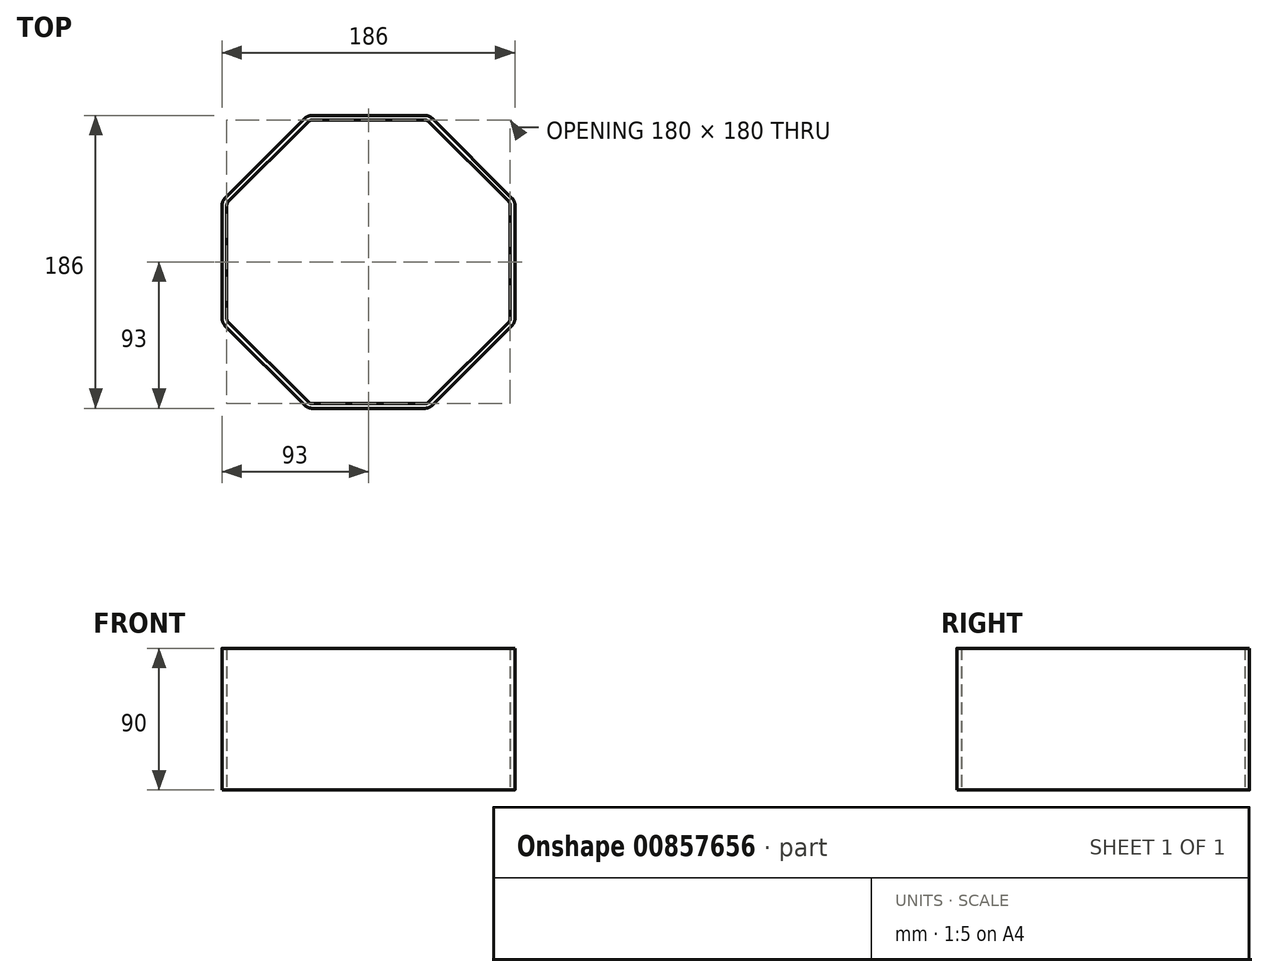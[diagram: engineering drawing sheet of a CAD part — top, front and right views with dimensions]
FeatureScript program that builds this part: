
annotation { "Feature Type Name" : "Feature", "Feature Type Description" : "" }
export const myFeature = defineFeature(function(context is Context, id is Id, definition is map)
    precondition{}
    {
        {
            var Q0;
            Q0=qCreatedBy(makeId("Top.planeOp"),FACE);
            var sketch = newSketch(context, id + "F0", { "sketchPlane" : qUnion([Q0])});
            skCircle(sketch, "E0.cCircle", {"center": v(0, 0) * mm, "radius": 90 * mm, "construction": true});
            skLineSegment(sketch, "E0.0", {"start": v(-37.28, 90) * mm, "end": v(37.28, 90) * mm});
            skLineSegment(sketch, "E0.1", {"start": v(37.28, 90) * mm, "end": v(90, 37.28) * mm});
            skLineSegment(sketch, "E0.2", {"start": v(90, 37.28) * mm, "end": v(90, -37.28) * mm});
            skLineSegment(sketch, "E0.3", {"start": v(90, -37.28) * mm, "end": v(37.28, -90) * mm});
            skLineSegment(sketch, "E0.4", {"start": v(37.28, -90) * mm, "end": v(-37.28, -90) * mm});
            skLineSegment(sketch, "E0.5", {"start": v(-37.28, -90) * mm, "end": v(-90, -37.28) * mm});
            skLineSegment(sketch, "E0.6", {"start": v(-90, -37.28) * mm, "end": v(-90, 37.28) * mm});
            skLineSegment(sketch, "E0.7", {"start": v(-90, 37.28) * mm, "end": v(-37.28, 90) * mm});
            skPoint(sketch, "E0.0.midPoint", {"position": v(0, 90) * mm});
            skLineSegment(sketch, "E1.0", {"start": v(38.52, 93) * mm, "end": v(93, 38.52) * mm});
            skLineSegment(sketch, "E1.1", {"start": v(-38.52, 93) * mm, "end": v(38.52, 93) * mm});
            skLineSegment(sketch, "E1.2", {"start": v(93, 38.52) * mm, "end": v(93, -38.52) * mm});
            skLineSegment(sketch, "E1.3", {"start": v(-93, 38.52) * mm, "end": v(-38.52, 93) * mm});
            skLineSegment(sketch, "E1.4", {"start": v(93, -38.52) * mm, "end": v(38.52, -93) * mm});
            skLineSegment(sketch, "E1.5", {"start": v(38.52, -93) * mm, "end": v(-38.52, -93) * mm});
            skLineSegment(sketch, "E1.6", {"start": v(-38.52, -93) * mm, "end": v(-93, -38.52) * mm});
            skLineSegment(sketch, "E1.7", {"start": v(-93, -38.52) * mm, "end": v(-93, 38.52) * mm});
            skSolve(sketch);
        }
        {
            var Q0;
            Q0 = qSketchRegion(id + "F0", true);
            extrude(context, id + "F1", {"entities" : qUnion([Q0]), "depth" : 90 * mm, "offsetDistance" : 25 * mm});
        }
        {
            var Q0;
            Q0=makeQuery(id+"F1.opExtrude","SWEPT_EDGE",EDGE,{"disambiguationData":[OSD([sQuery(id+"F0.wireOp",EDGE,"E0.0"),sQuery(id+"F0.wireOp",EDGE,"E0.7")])]});
            var Q1;
            Q1=makeQuery(id+"F1.opExtrude","SWEPT_EDGE",EDGE,{"disambiguationData":[OSD([sQuery(id+"F0.wireOp",EDGE,"E0.0"),sQuery(id+"F0.wireOp",EDGE,"E0.1")])]});
            var Q2;
            Q2=makeQuery(id+"F1.opExtrude","SWEPT_EDGE",EDGE,{"disambiguationData":[OSD([sQuery(id+"F0.wireOp",EDGE,"E0.1"),sQuery(id+"F0.wireOp",EDGE,"E0.2")])]});
            var Q3;
            Q3=makeQuery(id+"F1.opExtrude","SWEPT_EDGE",EDGE,{"disambiguationData":[OSD([sQuery(id+"F0.wireOp",EDGE,"E0.2"),sQuery(id+"F0.wireOp",EDGE,"E0.3")])]});
            var Q4;
            Q4=makeQuery(id+"F1.opExtrude","SWEPT_EDGE",EDGE,{"disambiguationData":[OSD([sQuery(id+"F0.wireOp",EDGE,"E0.3"),sQuery(id+"F0.wireOp",EDGE,"E0.4")])]});
            var Q5;
            Q5=makeQuery(id+"F1.opExtrude","SWEPT_EDGE",EDGE,{"disambiguationData":[OSD([sQuery(id+"F0.wireOp",EDGE,"E0.4"),sQuery(id+"F0.wireOp",EDGE,"E0.5")])]});
            var Q6;
            Q6=makeQuery(id+"F1.opExtrude","SWEPT_EDGE",EDGE,{"disambiguationData":[OSD([sQuery(id+"F0.wireOp",EDGE,"E0.5"),sQuery(id+"F0.wireOp",EDGE,"E0.6")])]});
            var Q7;
            Q7=makeQuery(id+"F1.opExtrude","SWEPT_EDGE",EDGE,{"disambiguationData":[OSD([sQuery(id+"F0.wireOp",EDGE,"E0.6"),sQuery(id+"F0.wireOp",EDGE,"E0.7")])]});
            fillet(context, id + "F2", {"entities" : qUnion([Q0, Q1, Q2, Q3, Q4, Q5, Q6, Q7]), "radius" : 3 * mm, "tangentPropagation" : true, "allowEdgeOverflow" : false});
        }
        {
            var Q0;
            Q0=makeQuery(id+"F1.opExtrude","SWEPT_EDGE",EDGE,{"disambiguationData":[OSD([sQuery(id+"F0.wireOp",EDGE,"E1.6"),sQuery(id+"F0.wireOp",EDGE,"E1.7")])]});
            var Q1;
            Q1=makeQuery(id+"F1.opExtrude","SWEPT_EDGE",EDGE,{"disambiguationData":[OSD([sQuery(id+"F0.wireOp",EDGE,"E1.5"),sQuery(id+"F0.wireOp",EDGE,"E1.6")])]});
            var Q2;
            Q2=makeQuery(id+"F1.opExtrude","SWEPT_EDGE",EDGE,{"disambiguationData":[OSD([sQuery(id+"F0.wireOp",EDGE,"E1.4"),sQuery(id+"F0.wireOp",EDGE,"E1.5")])]});
            var Q3;
            Q3=makeQuery(id+"F1.opExtrude","SWEPT_EDGE",EDGE,{"disambiguationData":[OSD([sQuery(id+"F0.wireOp",EDGE,"E1.2"),sQuery(id+"F0.wireOp",EDGE,"E1.4")])]});
            var Q4;
            Q4=makeQuery(id+"F1.opExtrude","SWEPT_EDGE",EDGE,{"disambiguationData":[OSD([sQuery(id+"F0.wireOp",EDGE,"E1.0"),sQuery(id+"F0.wireOp",EDGE,"E1.2")])]});
            var Q5;
            Q5=makeQuery(id+"F1.opExtrude","SWEPT_EDGE",EDGE,{"disambiguationData":[OSD([sQuery(id+"F0.wireOp",EDGE,"E1.0"),sQuery(id+"F0.wireOp",EDGE,"E1.1")])]});
            var Q6;
            Q6=makeQuery(id+"F1.opExtrude","SWEPT_EDGE",EDGE,{"disambiguationData":[OSD([sQuery(id+"F0.wireOp",EDGE,"E1.1"),sQuery(id+"F0.wireOp",EDGE,"E1.3")])]});
            var Q7;
            Q7=makeQuery(id+"F1.opExtrude","SWEPT_EDGE",EDGE,{"disambiguationData":[OSD([sQuery(id+"F0.wireOp",EDGE,"E1.3"),sQuery(id+"F0.wireOp",EDGE,"E1.7")])]});
            fillet(context, id + "F3", {"entities" : qUnion([Q0, Q1, Q2, Q3, Q4, Q5, Q6, Q7]), "radius" : 6 * mm, "tangentPropagation" : true, "allowEdgeOverflow" : false});
        }
    });
